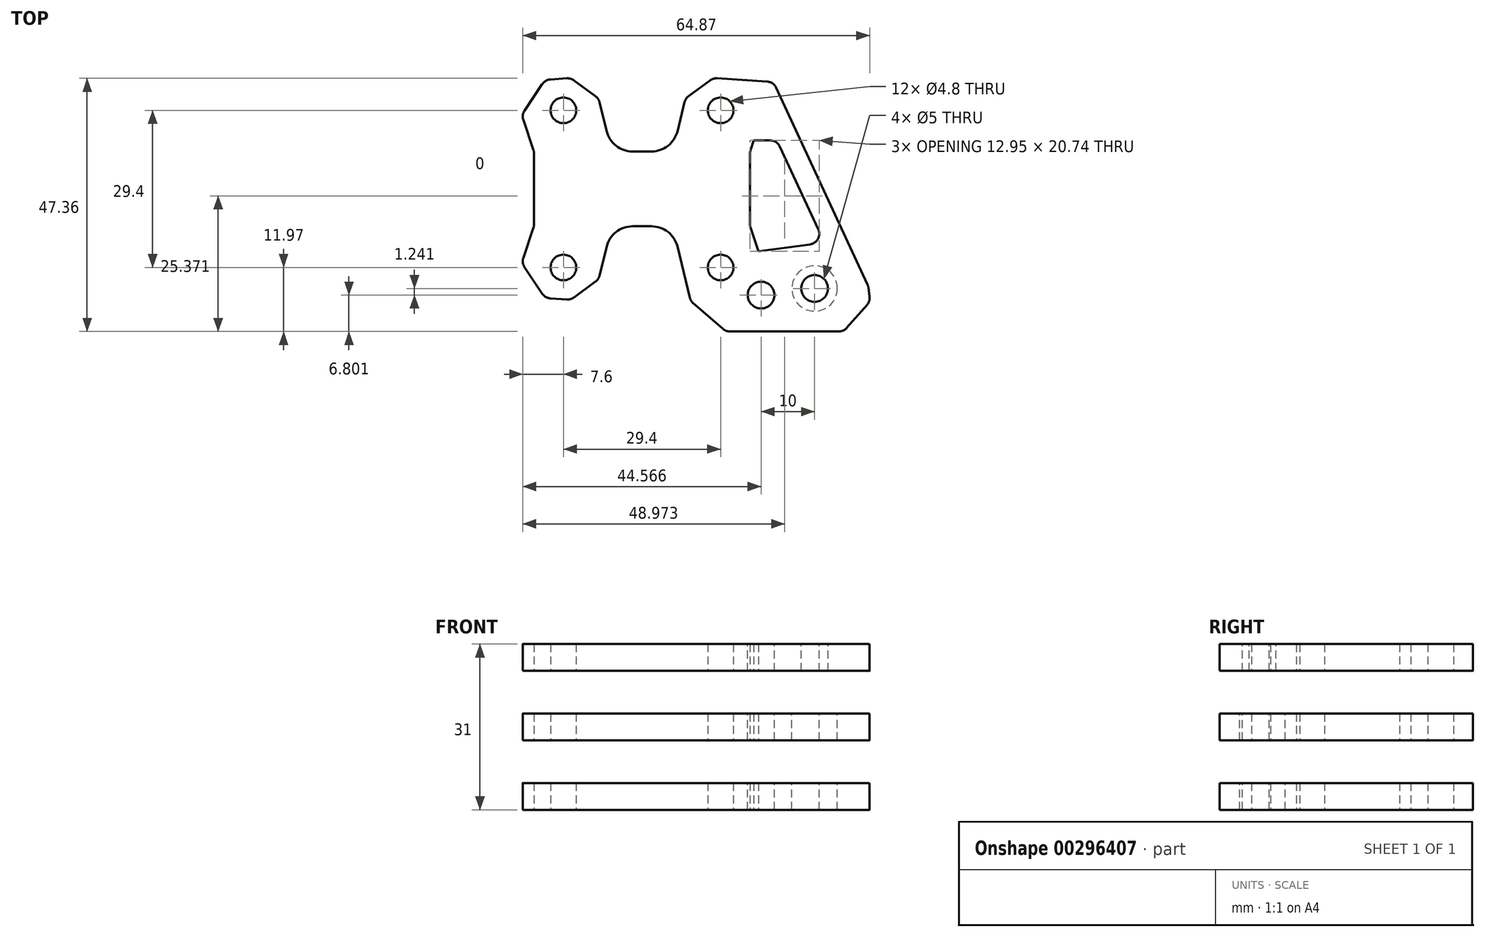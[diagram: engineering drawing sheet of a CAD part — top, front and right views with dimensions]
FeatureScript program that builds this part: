
annotation { "Feature Type Name" : "Feature", "Feature Type Description" : "" }
export const myFeature = defineFeature(function(context is Context, id is Id, definition is map)
    precondition{}
    {
        {
            var Q0;
            Q0=qCreatedBy(makeId("Top.planeOp"),FACE);
            var sketch = newSketch(context, id + "F0", { "sketchPlane" : qUnion([Q0])});
            skLineSegment(sketch, "E0.bottom", {"start": v(14.7, -14.7) * mm, "end": v(-14.7, -14.7) * mm, "construction": true});
            skLineSegment(sketch, "E0.top", {"start": v(14.7, 14.7) * mm, "end": v(-14.7, 14.7) * mm, "construction": true});
            skLineSegment(sketch, "E0.left", {"start": v(14.7, -14.7) * mm, "end": v(14.7, 14.7) * mm, "construction": true});
            skLineSegment(sketch, "E0.right", {"start": v(-14.7, -14.7) * mm, "end": v(-14.7, 14.7) * mm, "construction": true});
            skPoint(sketch, "E0.middle", {"position": v(0, 0) * mm});
            skLineSegment(sketch, "E1", {"start": v(-14.7, 5) * mm, "end": v(14.7, 5) * mm, "construction": true});
            skLineSegment(sketch, "E2.MirrorCS", {"start": v(-14.7, -5) * mm, "end": v(14.7, -5) * mm, "construction": true});
            skCircle(sketch, "E3", {"center": v(14.7, 14.7) * mm, "radius": 2.5 * mm, "construction": true});
            skCircle(sketch, "E4", {"center": v(14.7, 14.7) * mm, "radius": 9.7 * mm, "construction": true});
            skCircle(sketch, "E5.MirrorC", {"center": v(14.7, -14.7) * mm, "radius": 2.5 * mm, "construction": true});
            skCircle(sketch, "E6.MirrorC", {"center": v(14.7, -14.7) * mm, "radius": 9.7 * mm, "construction": true});
            skCircle(sketch, "E7.MirrorC", {"center": v(-14.7, 14.7) * mm, "radius": 9.7 * mm, "construction": true});
            skCircle(sketch, "E8.MirrorC", {"center": v(-14.7, 14.7) * mm, "radius": 2.5 * mm, "construction": true});
            skCircle(sketch, "E9.MirrorC", {"center": v(-14.7, -14.7) * mm, "radius": 9.7 * mm, "construction": true});
            skCircle(sketch, "E10.MirrorC", {"center": v(-14.7, -14.7) * mm, "radius": 2.5 * mm, "construction": true});
            skLineSegment(sketch, "E11", {"start": v(0, 7) * mm, "end": v(5.7, 7) * mm});
            skLineSegment(sketch, "E12", {"start": v(5.7, 7) * mm, "end": v(9.11, 21) * mm});
            skLineSegment(sketch, "E13", {"start": v(9.11, 21) * mm, "end": v(24.6, 20) * mm});
            skLineSegment(sketch, "E14", {"start": v(24.6, 20) * mm, "end": v(20.2, 7) * mm});
            skLineSegment(sketch, "E15", {"start": v(20.2, 7) * mm, "end": v(20.2, 0) * mm});
            skLineSegment(sketch, "E16", {"start": v(20.2, 0) * mm, "end": v(0, 0) * mm});
            skLineSegment(sketch, "E17", {"start": v(0, 7) * mm, "end": v(0, 0) * mm});
            skCircle(sketch, "E18", {"center": v(14.7, 14.7) * mm, "radius": 2.4 * mm});
            skSolve(sketch);
        }
        {
            var Q0;
            Q0=makeQuery(id+"F0.imprint","IMPRINT",FACE,{"disambiguationData":[TD([[makeQuery(id+"F0.imprint","IMPRINT",EDGE,{"derivedFrom":sQuery(id+"F0.wireOp",EDGE,"E11")}),-1.0]])]});
            extrude(context, id + "F1", {"entities" : qUnion([Q0]), "depth" : 5 * mm, "offsetDistance" : 25 * mm});
        }
        {
            var Q0;
            Q0=makeQuery(id+"F1.opExtrude","SWEPT_BODY",BODY,{"disambiguationData":[OSD([sQuery(id+"F0.wireOp",EDGE,"E11"),sQuery(id+"F0.wireOp",EDGE,"E12"),sQuery(id+"F0.wireOp",EDGE,"E13"),sQuery(id+"F0.wireOp",EDGE,"E14"),sQuery(id+"F0.wireOp",EDGE,"E15"),sQuery(id+"F0.wireOp",EDGE,"E16"),sQuery(id+"F0.wireOp",EDGE,"E17"),sQuery(id+"F0.wireOp",EDGE,"E18")])]});
            var Q1;
            Q1=makeQuery(id+"F1.opExtrude","SWEPT_FACE",FACE,{"disambiguationData":[OSD([sQuery(id+"F0.wireOp",EDGE,"E16")])]});
            mirror(context, id + "F2", {"operationType" : NewBodyOperationType.ADD, "entities" : qUnion([Q0]), "mirrorPlane" : qUnion([Q1])});
        }
        {
            var Q0;
            Q0=makeQuery(id+"F1.opExtrude","SWEPT_BODY",BODY,{"disambiguationData":[OSD([sQuery(id+"F0.wireOp",EDGE,"E11"),sQuery(id+"F0.wireOp",EDGE,"E12"),sQuery(id+"F0.wireOp",EDGE,"E13"),sQuery(id+"F0.wireOp",EDGE,"E14"),sQuery(id+"F0.wireOp",EDGE,"E15"),sQuery(id+"F0.wireOp",EDGE,"E16"),sQuery(id+"F0.wireOp",EDGE,"E17"),sQuery(id+"F0.wireOp",EDGE,"E18")])]});
            var Q1;
            {var subQ0=makeQuery(id+"F1.opExtrude","SWEPT_FACE",FACE,{"disambiguationData":[OSD([sQuery(id+"F0.wireOp",EDGE,"E17")])]});Q1=makeQuery(id+"F2.boolean.opBoolean","MERGE",FACE,{"derivedFrom":[subQ0,makeQuery(id+"F2.opPattern","COPY",FACE,{"derivedFrom":subQ0,"instanceName":"1"})]});}
            mirror(context, id + "F3", {"operationType" : NewBodyOperationType.ADD, "entities" : qUnion([Q0]), "mirrorPlane" : qUnion([Q1])});
        }
        {
            var Q0;
            Q0=qCreatedBy(makeId("Top.planeOp"),FACE);
            var sketch = newSketch(context, id + "F4", { "sketchPlane" : qUnion([Q0])});
            skLineSegment(sketch, "E19", {"start": v(0, 0) * mm, "end": v(45.1, -26.03) * mm, "construction": true});
            skPoint(sketch, "E20", {"position": v(32.27, -18.63) * mm});
            skCircle(sketch, "E21", {"center": v(32.27, -18.63) * mm, "radius": 5 * mm, "construction": true});
            skCircle(sketch, "E22", {"center": v(14.7, -14.7) * mm, "radius": 12 * mm, "construction": true});
            skLineSegment(sketch, "E23", {"start": v(24.6, 20) * mm, "end": v(42.3, -18.19) * mm});
            skLineSegment(sketch, "E24", {"start": v(42.3, -18.19) * mm, "end": v(43.42, -26.67) * mm});
            skLineSegment(sketch, "E25", {"start": v(43.42, -26.67) * mm, "end": v(15.65, -26.67) * mm});
            skLineSegment(sketch, "E26", {"start": v(15.65, -26.67) * mm, "end": v(9.11, -21) * mm});
            skLineSegment(sketch, "E27", {"start": v(25.26, 9.07) * mm, "end": v(34.1, -10.02) * mm});
            skLineSegment(sketch, "E28", {"start": v(34.1, -10.02) * mm, "end": v(21.78, -11.67) * mm});
            skLineSegment(sketch, "E29", {"start": v(25.26, 9.07) * mm, "end": v(20.9, 9.07) * mm});
            skLineSegment(sketch, "E30", {"start": v(24.6, 20) * mm, "end": v(20.9, 9.07) * mm});
            skLineSegment(sketch, "E31", {"start": v(9.11, -21) * mm, "end": v(20.23, -18.7) * mm});
            skLineSegment(sketch, "E32", {"start": v(20.23, -18.7) * mm, "end": v(21.78, -11.67) * mm});
            skSolve(sketch);
        }
        {
            var Q0;
            Q0=makeQuery(id+"F4.imprint","IMPRINT",FACE,{"disambiguationData":[TD([[makeQuery(id+"F4.imprint","IMPRINT",EDGE,{"derivedFrom":sQuery(id+"F4.wireOp",EDGE,"E23")}),-1.0]])]});
            var Q1;
            {var subQ0=makeQuery(id+"F1.opExtrude","CAP_FACE",FACE,{"disambiguationData":[OSD([sQuery(id+"F0.wireOp",EDGE,"E11"),sQuery(id+"F0.wireOp",EDGE,"E12"),sQuery(id+"F0.wireOp",EDGE,"E13"),sQuery(id+"F0.wireOp",EDGE,"E14"),sQuery(id+"F0.wireOp",EDGE,"E15"),sQuery(id+"F0.wireOp",EDGE,"E16"),sQuery(id+"F0.wireOp",EDGE,"E17"),sQuery(id+"F0.wireOp",EDGE,"E18")])],"isStart":false});var subQ1=makeQuery(id+"F2.boolean.opBoolean","MERGE",FACE,{"derivedFrom":[subQ0,makeQuery(id+"F2.opPattern","COPY",FACE,{"derivedFrom":subQ0,"instanceName":"1"})]});Q1=makeQuery(id+"F3.boolean.opBoolean","MERGE",FACE,{"derivedFrom":[subQ1,makeQuery(id+"F3.opPattern","COPY",FACE,{"derivedFrom":subQ1,"instanceName":"1"})]});}
            extrude(context, id + "F5", {"entities" : qUnion([Q0]), "operationType" : NewBodyOperationType.ADD, "endBound" : BoundingType.UP_TO_SURFACE, "depth" : 25 * mm, "endBoundEntityFace" : qUnion([Q1]), "offsetDistance" : 25 * mm});
        }
        {
            var Q0;
            Q0=makeQuery(id+"F3.opPattern","COPY",EDGE,{"derivedFrom":makeQuery(id+"F1.opExtrude","SWEPT_EDGE",EDGE,{"disambiguationData":[OSD([sQuery(id+"F0.wireOp",EDGE,"E13"),sQuery(id+"F0.wireOp",EDGE,"E14")])]}),"instanceName":"1"});
            var Q1;
            Q1=makeQuery(id+"F3.opPattern","COPY",EDGE,{"derivedFrom":makeQuery(id+"F2.opPattern","COPY",EDGE,{"derivedFrom":makeQuery(id+"F1.opExtrude","SWEPT_EDGE",EDGE,{"disambiguationData":[OSD([sQuery(id+"F0.wireOp",EDGE,"E13"),sQuery(id+"F0.wireOp",EDGE,"E14")])]}),"instanceName":"1"}),"instanceName":"1"});
            var Q2;
            Q2=makeQuery(id+"F3.opPattern","COPY",EDGE,{"derivedFrom":makeQuery(id+"F2.opPattern","COPY",EDGE,{"derivedFrom":makeQuery(id+"F1.opExtrude","SWEPT_EDGE",EDGE,{"disambiguationData":[OSD([sQuery(id+"F0.wireOp",EDGE,"E12"),sQuery(id+"F0.wireOp",EDGE,"E13")])]}),"instanceName":"1"}),"instanceName":"1"});
            var Q3;
            Q3=makeQuery(id+"F3.opPattern","COPY",EDGE,{"derivedFrom":makeQuery(id+"F1.opExtrude","SWEPT_EDGE",EDGE,{"disambiguationData":[OSD([sQuery(id+"F0.wireOp",EDGE,"E12"),sQuery(id+"F0.wireOp",EDGE,"E13")])]}),"instanceName":"1"});
            var Q4;
            Q4=makeQuery(id+"F1.opExtrude","SWEPT_EDGE",EDGE,{"disambiguationData":[OSD([sQuery(id+"F0.wireOp",EDGE,"E12"),sQuery(id+"F0.wireOp",EDGE,"E13")])]});
            var Q5;
            Q5=makeQuery(id+"F5.opExtrude","SWEPT_EDGE",EDGE,{"disambiguationData":[OSD([sQuery(id+"F4.wireOp",EDGE,"E24"),sQuery(id+"F4.wireOp",EDGE,"E25")])]});
            chamfer(context, id + "F6", {"entities" : qUnion([Q0, Q1, Q2, Q3, Q4, Q5]), "width" : 5 * mm, "tangentPropagation" : true});
        }
        {
            var Q0;
            Q0=makeQuery(id+"F3.opPattern","COPY",EDGE,{"derivedFrom":makeQuery(id+"F1.opExtrude","SWEPT_EDGE",EDGE,{"disambiguationData":[OSD([sQuery(id+"F0.wireOp",EDGE,"E11"),sQuery(id+"F0.wireOp",EDGE,"E12")])]}),"instanceName":"1"});
            var Q1;
            Q1=makeQuery(id+"F1.opExtrude","SWEPT_EDGE",EDGE,{"disambiguationData":[OSD([sQuery(id+"F0.wireOp",EDGE,"E11"),sQuery(id+"F0.wireOp",EDGE,"E12")])]});
            var Q2;
            Q2=makeQuery(id+"F2.opPattern","COPY",EDGE,{"derivedFrom":makeQuery(id+"F1.opExtrude","SWEPT_EDGE",EDGE,{"disambiguationData":[OSD([sQuery(id+"F0.wireOp",EDGE,"E11"),sQuery(id+"F0.wireOp",EDGE,"E12")])]}),"instanceName":"1"});
            var Q3;
            Q3=makeQuery(id+"F3.opPattern","COPY",EDGE,{"derivedFrom":makeQuery(id+"F2.opPattern","COPY",EDGE,{"derivedFrom":makeQuery(id+"F1.opExtrude","SWEPT_EDGE",EDGE,{"disambiguationData":[OSD([sQuery(id+"F0.wireOp",EDGE,"E11"),sQuery(id+"F0.wireOp",EDGE,"E12")])]}),"instanceName":"1"}),"instanceName":"1"});
            fillet(context, id + "F7", {"entities" : qUnion([Q0, Q1, Q2, Q3]), "radius" : 5 * mm, "tangentPropagation" : true, "allowEdgeOverflow" : false});
        }
        {
            var Q0;
            {var subQ0=sQuery(id+"F0.wireOp",EDGE,"E14");Q0=makeQuery(id+"F6.opChamfer","BLEND_EDGE",EDGE,{"blendedFrom":[makeQuery(id+"F3.opPattern","COPY",EDGE,{"derivedFrom":makeQuery(id+"F1.opExtrude","SWEPT_EDGE",EDGE,{"disambiguationData":[OSD([sQuery(id+"F0.wireOp",EDGE,"E13"),subQ0])]}),"instanceName":"1"}),makeQuery(id+"F3.opPattern","COPY",FACE,{"derivedFrom":makeQuery(id+"F1.opExtrude","SWEPT_FACE",FACE,{"disambiguationData":[OSD([subQ0])]}),"instanceName":"1"})],"blendedInto":[makeQuery(id+"F3.opPattern","COPY",FACE,{"derivedFrom":makeQuery(id+"F1.opExtrude","SWEPT_FACE",FACE,{"disambiguationData":[OSD([subQ0])]}),"instanceName":"1"})]});}
            var Q1;
            Q1=makeQuery(id+"F3.opPattern","COPY",EDGE,{"derivedFrom":makeQuery(id+"F1.opExtrude","SWEPT_EDGE",EDGE,{"disambiguationData":[OSD([sQuery(id+"F0.wireOp",EDGE,"E14"),sQuery(id+"F0.wireOp",EDGE,"E15")])]}),"instanceName":"1"});
            var Q2;
            Q2=makeQuery(id+"F3.opPattern","COPY",EDGE,{"derivedFrom":makeQuery(id+"F2.opPattern","COPY",EDGE,{"derivedFrom":makeQuery(id+"F1.opExtrude","SWEPT_EDGE",EDGE,{"disambiguationData":[OSD([sQuery(id+"F0.wireOp",EDGE,"E14"),sQuery(id+"F0.wireOp",EDGE,"E15")])]}),"instanceName":"1"}),"instanceName":"1"});
            var Q3;
            {var subQ0=sQuery(id+"F0.wireOp",EDGE,"E14");Q3=makeQuery(id+"F6.opChamfer","BLEND_EDGE",EDGE,{"blendedFrom":[makeQuery(id+"F3.opPattern","COPY",EDGE,{"derivedFrom":makeQuery(id+"F2.opPattern","COPY",EDGE,{"derivedFrom":makeQuery(id+"F1.opExtrude","SWEPT_EDGE",EDGE,{"disambiguationData":[OSD([sQuery(id+"F0.wireOp",EDGE,"E13"),subQ0])]}),"instanceName":"1"}),"instanceName":"1"}),makeQuery(id+"F3.opPattern","COPY",FACE,{"derivedFrom":makeQuery(id+"F2.opPattern","COPY",FACE,{"derivedFrom":makeQuery(id+"F1.opExtrude","SWEPT_FACE",FACE,{"disambiguationData":[OSD([subQ0])]}),"instanceName":"1"}),"instanceName":"1"})],"blendedInto":[makeQuery(id+"F3.opPattern","COPY",FACE,{"derivedFrom":makeQuery(id+"F2.opPattern","COPY",FACE,{"derivedFrom":makeQuery(id+"F1.opExtrude","SWEPT_FACE",FACE,{"disambiguationData":[OSD([subQ0])]}),"instanceName":"1"}),"instanceName":"1"})]});}
            var Q4;
            {var subQ0=sQuery(id+"F0.wireOp",EDGE,"E13");Q4=makeQuery(id+"F6.opChamfer","BLEND_EDGE",EDGE,{"blendedFrom":[makeQuery(id+"F3.opPattern","COPY",EDGE,{"derivedFrom":makeQuery(id+"F2.opPattern","COPY",EDGE,{"derivedFrom":makeQuery(id+"F1.opExtrude","SWEPT_EDGE",EDGE,{"disambiguationData":[OSD([subQ0,sQuery(id+"F0.wireOp",EDGE,"E14")])]}),"instanceName":"1"}),"instanceName":"1"}),makeQuery(id+"F3.opPattern","COPY",FACE,{"derivedFrom":makeQuery(id+"F2.opPattern","COPY",FACE,{"derivedFrom":makeQuery(id+"F1.opExtrude","SWEPT_FACE",FACE,{"disambiguationData":[OSD([subQ0])]}),"instanceName":"1"}),"instanceName":"1"})],"blendedInto":[makeQuery(id+"F3.opPattern","COPY",FACE,{"derivedFrom":makeQuery(id+"F2.opPattern","COPY",FACE,{"derivedFrom":makeQuery(id+"F1.opExtrude","SWEPT_FACE",FACE,{"disambiguationData":[OSD([subQ0])]}),"instanceName":"1"}),"instanceName":"1"})]});}
            var Q5;
            {var subQ0=sQuery(id+"F0.wireOp",EDGE,"E13");Q5=makeQuery(id+"F6.opChamfer","BLEND_EDGE",EDGE,{"blendedFrom":[makeQuery(id+"F3.opPattern","COPY",EDGE,{"derivedFrom":makeQuery(id+"F2.opPattern","COPY",EDGE,{"derivedFrom":makeQuery(id+"F1.opExtrude","SWEPT_EDGE",EDGE,{"disambiguationData":[OSD([sQuery(id+"F0.wireOp",EDGE,"E12"),subQ0])]}),"instanceName":"1"}),"instanceName":"1"}),makeQuery(id+"F3.opPattern","COPY",FACE,{"derivedFrom":makeQuery(id+"F2.opPattern","COPY",FACE,{"derivedFrom":makeQuery(id+"F1.opExtrude","SWEPT_FACE",FACE,{"disambiguationData":[OSD([subQ0])]}),"instanceName":"1"}),"instanceName":"1"})],"blendedInto":[makeQuery(id+"F3.opPattern","COPY",FACE,{"derivedFrom":makeQuery(id+"F2.opPattern","COPY",FACE,{"derivedFrom":makeQuery(id+"F1.opExtrude","SWEPT_FACE",FACE,{"disambiguationData":[OSD([subQ0])]}),"instanceName":"1"}),"instanceName":"1"})]});}
            var Q6;
            {var subQ0=sQuery(id+"F0.wireOp",EDGE,"E12");Q6=makeQuery(id+"F6.opChamfer","BLEND_EDGE",EDGE,{"blendedFrom":[makeQuery(id+"F3.opPattern","COPY",EDGE,{"derivedFrom":makeQuery(id+"F2.opPattern","COPY",EDGE,{"derivedFrom":makeQuery(id+"F1.opExtrude","SWEPT_EDGE",EDGE,{"disambiguationData":[OSD([subQ0,sQuery(id+"F0.wireOp",EDGE,"E13")])]}),"instanceName":"1"}),"instanceName":"1"}),makeQuery(id+"F3.opPattern","COPY",FACE,{"derivedFrom":makeQuery(id+"F2.opPattern","COPY",FACE,{"derivedFrom":makeQuery(id+"F1.opExtrude","SWEPT_FACE",FACE,{"disambiguationData":[OSD([subQ0])]}),"instanceName":"1"}),"instanceName":"1"})],"blendedInto":[makeQuery(id+"F3.opPattern","COPY",FACE,{"derivedFrom":makeQuery(id+"F2.opPattern","COPY",FACE,{"derivedFrom":makeQuery(id+"F1.opExtrude","SWEPT_FACE",FACE,{"disambiguationData":[OSD([subQ0])]}),"instanceName":"1"}),"instanceName":"1"})]});}
            var Q7;
            Q7=makeQuery(id+"F5.boolean.opBoolean","MERGE",EDGE,{"derivedFrom":[makeQuery(id+"F2.opPattern","COPY",EDGE,{"derivedFrom":makeQuery(id+"F1.opExtrude","SWEPT_EDGE",EDGE,{"disambiguationData":[OSD([sQuery(id+"F0.wireOp",EDGE,"E12"),sQuery(id+"F0.wireOp",EDGE,"E13")])]}),"instanceName":"1"}),makeQuery(id+"F5.opExtrude","SWEPT_EDGE",EDGE,{"disambiguationData":[OSD([sQuery(id+"F4.wireOp",EDGE,"E26"),sQuery(id+"F4.wireOp",EDGE,"E31")])]})]});
            var Q8;
            Q8=makeQuery(id+"F5.opExtrude","SWEPT_EDGE",EDGE,{"disambiguationData":[OSD([sQuery(id+"F4.wireOp",EDGE,"E25"),sQuery(id+"F4.wireOp",EDGE,"E26")])]});
            var Q9;
            {var subQ0=sQuery(id+"F4.wireOp",EDGE,"E25");Q9=makeQuery(id+"F6.opChamfer","BLEND_EDGE",EDGE,{"blendedFrom":[makeQuery(id+"F5.opExtrude","SWEPT_EDGE",EDGE,{"disambiguationData":[OSD([sQuery(id+"F4.wireOp",EDGE,"E24"),subQ0])]}),makeQuery(id+"F5.opExtrude","SWEPT_FACE",FACE,{"disambiguationData":[OSD([subQ0])]})],"blendedInto":[makeQuery(id+"F5.opExtrude","SWEPT_FACE",FACE,{"disambiguationData":[OSD([subQ0])]})]});}
            var Q10;
            {var subQ0=sQuery(id+"F4.wireOp",EDGE,"E24");Q10=makeQuery(id+"F6.opChamfer","BLEND_EDGE",EDGE,{"blendedFrom":[makeQuery(id+"F5.opExtrude","SWEPT_EDGE",EDGE,{"disambiguationData":[OSD([subQ0,sQuery(id+"F4.wireOp",EDGE,"E25")])]}),makeQuery(id+"F5.opExtrude","SWEPT_FACE",FACE,{"disambiguationData":[OSD([subQ0])]})],"blendedInto":[makeQuery(id+"F5.opExtrude","SWEPT_FACE",FACE,{"disambiguationData":[OSD([subQ0])]})]});}
            var Q11;
            Q11=makeQuery(id+"F5.opExtrude","SWEPT_EDGE",EDGE,{"disambiguationData":[OSD([sQuery(id+"F4.wireOp",EDGE,"E23"),sQuery(id+"F4.wireOp",EDGE,"E24")])]});
            var Q12;
            Q12=makeQuery(id+"F5.boolean.opBoolean","MERGE",EDGE,{"derivedFrom":[makeQuery(id+"F1.opExtrude","SWEPT_EDGE",EDGE,{"disambiguationData":[OSD([sQuery(id+"F0.wireOp",EDGE,"E13"),sQuery(id+"F0.wireOp",EDGE,"E14")])]}),makeQuery(id+"F5.opExtrude","SWEPT_EDGE",EDGE,{"disambiguationData":[OSD([sQuery(id+"F4.wireOp",EDGE,"E23"),sQuery(id+"F4.wireOp",EDGE,"E30")])]})]});
            var Q13;
            {var subQ0=sQuery(id+"F0.wireOp",EDGE,"E13");Q13=makeQuery(id+"F6.opChamfer","BLEND_EDGE",EDGE,{"blendedFrom":[makeQuery(id+"F1.opExtrude","SWEPT_EDGE",EDGE,{"disambiguationData":[OSD([sQuery(id+"F0.wireOp",EDGE,"E12"),subQ0])]}),makeQuery(id+"F1.opExtrude","SWEPT_FACE",FACE,{"disambiguationData":[OSD([subQ0])]})],"blendedInto":[makeQuery(id+"F1.opExtrude","SWEPT_FACE",FACE,{"disambiguationData":[OSD([subQ0])]})]});}
            var Q14;
            {var subQ0=sQuery(id+"F0.wireOp",EDGE,"E12");Q14=makeQuery(id+"F6.opChamfer","BLEND_EDGE",EDGE,{"blendedFrom":[makeQuery(id+"F1.opExtrude","SWEPT_EDGE",EDGE,{"disambiguationData":[OSD([subQ0,sQuery(id+"F0.wireOp",EDGE,"E13")])]}),makeQuery(id+"F1.opExtrude","SWEPT_FACE",FACE,{"disambiguationData":[OSD([subQ0])]})],"blendedInto":[makeQuery(id+"F1.opExtrude","SWEPT_FACE",FACE,{"disambiguationData":[OSD([subQ0])]})]});}
            var Q15;
            {var subQ0=sQuery(id+"F0.wireOp",EDGE,"E12");Q15=makeQuery(id+"F6.opChamfer","BLEND_EDGE",EDGE,{"blendedFrom":[makeQuery(id+"F3.opPattern","COPY",EDGE,{"derivedFrom":makeQuery(id+"F1.opExtrude","SWEPT_EDGE",EDGE,{"disambiguationData":[OSD([subQ0,sQuery(id+"F0.wireOp",EDGE,"E13")])]}),"instanceName":"1"}),makeQuery(id+"F3.opPattern","COPY",FACE,{"derivedFrom":makeQuery(id+"F1.opExtrude","SWEPT_FACE",FACE,{"disambiguationData":[OSD([subQ0])]}),"instanceName":"1"})],"blendedInto":[makeQuery(id+"F3.opPattern","COPY",FACE,{"derivedFrom":makeQuery(id+"F1.opExtrude","SWEPT_FACE",FACE,{"disambiguationData":[OSD([subQ0])]}),"instanceName":"1"})]});}
            var Q16;
            {var subQ0=sQuery(id+"F0.wireOp",EDGE,"E13");Q16=makeQuery(id+"F6.opChamfer","BLEND_EDGE",EDGE,{"blendedFrom":[makeQuery(id+"F3.opPattern","COPY",EDGE,{"derivedFrom":makeQuery(id+"F1.opExtrude","SWEPT_EDGE",EDGE,{"disambiguationData":[OSD([sQuery(id+"F0.wireOp",EDGE,"E12"),subQ0])]}),"instanceName":"1"}),makeQuery(id+"F3.opPattern","COPY",FACE,{"derivedFrom":makeQuery(id+"F1.opExtrude","SWEPT_FACE",FACE,{"disambiguationData":[OSD([subQ0])]}),"instanceName":"1"})],"blendedInto":[makeQuery(id+"F3.opPattern","COPY",FACE,{"derivedFrom":makeQuery(id+"F1.opExtrude","SWEPT_FACE",FACE,{"disambiguationData":[OSD([subQ0])]}),"instanceName":"1"})]});}
            var Q17;
            {var subQ0=sQuery(id+"F0.wireOp",EDGE,"E13");Q17=makeQuery(id+"F6.opChamfer","BLEND_EDGE",EDGE,{"blendedFrom":[makeQuery(id+"F3.opPattern","COPY",EDGE,{"derivedFrom":makeQuery(id+"F1.opExtrude","SWEPT_EDGE",EDGE,{"disambiguationData":[OSD([subQ0,sQuery(id+"F0.wireOp",EDGE,"E14")])]}),"instanceName":"1"}),makeQuery(id+"F3.opPattern","COPY",FACE,{"derivedFrom":makeQuery(id+"F1.opExtrude","SWEPT_FACE",FACE,{"disambiguationData":[OSD([subQ0])]}),"instanceName":"1"})],"blendedInto":[makeQuery(id+"F3.opPattern","COPY",FACE,{"derivedFrom":makeQuery(id+"F1.opExtrude","SWEPT_FACE",FACE,{"disambiguationData":[OSD([subQ0])]}),"instanceName":"1"})]});}
            fillet(context, id + "F8", {"entities" : qUnion([Q0, Q1, Q2, Q3, Q4, Q5, Q6, Q7, Q8, Q9, Q10, Q11, Q12, Q13, Q14, Q15, Q16, Q17]), "radius" : 2 * mm, "tangentPropagation" : true, "allowEdgeOverflow" : false});
        }
        {
            var Q0;
            Q0=makeQuery(id+"F5.opExtrude","SWEPT_EDGE",EDGE,{"disambiguationData":[OSD([sQuery(id+"F4.wireOp",EDGE,"E29"),sQuery(id+"F4.wireOp",EDGE,"E30")])]});
            var Q1;
            Q1=makeQuery(id+"F2.opPattern","COPY",EDGE,{"derivedFrom":makeQuery(id+"F1.opExtrude","SWEPT_EDGE",EDGE,{"disambiguationData":[OSD([sQuery(id+"F0.wireOp",EDGE,"E14"),sQuery(id+"F0.wireOp",EDGE,"E15")])]}),"instanceName":"1"});
            var Q2;
            Q2=makeQuery(id+"F5.opExtrude","SWEPT_EDGE",EDGE,{"disambiguationData":[OSD([sQuery(id+"F4.wireOp",EDGE,"E28"),sQuery(id+"F4.wireOp",EDGE,"E32")])]});
            var Q3;
            Q3=makeQuery(id+"F5.opExtrude","SWEPT_EDGE",EDGE,{"disambiguationData":[OSD([sQuery(id+"F4.wireOp",EDGE,"E27"),sQuery(id+"F4.wireOp",EDGE,"E28")])]});
            var Q4;
            Q4=makeQuery(id+"F5.opExtrude","SWEPT_EDGE",EDGE,{"disambiguationData":[OSD([sQuery(id+"F4.wireOp",EDGE,"E27"),sQuery(id+"F4.wireOp",EDGE,"E29")])]});
            var Q5;
            Q5=makeQuery(id+"F1.opExtrude","SWEPT_EDGE",EDGE,{"disambiguationData":[OSD([sQuery(id+"F0.wireOp",EDGE,"E14"),sQuery(id+"F0.wireOp",EDGE,"E15")])]});
            fillet(context, id + "F9", {"entities" : qUnion([Q0, Q1, Q2, Q3, Q4, Q5]), "radius" : 2 * mm, "tangentPropagation" : true, "allowEdgeOverflow" : false});
        }
        {
            var Q0;
            {var subQ0=makeQuery(id+"F1.opExtrude","CAP_FACE",FACE,{"disambiguationData":[OSD([sQuery(id+"F0.wireOp",EDGE,"E11"),sQuery(id+"F0.wireOp",EDGE,"E12"),sQuery(id+"F0.wireOp",EDGE,"E13"),sQuery(id+"F0.wireOp",EDGE,"E14"),sQuery(id+"F0.wireOp",EDGE,"E15"),sQuery(id+"F0.wireOp",EDGE,"E16"),sQuery(id+"F0.wireOp",EDGE,"E17"),sQuery(id+"F0.wireOp",EDGE,"E18")])],"isStart":false});var subQ1=makeQuery(id+"F2.boolean.opBoolean","MERGE",FACE,{"derivedFrom":[subQ0,makeQuery(id+"F2.opPattern","COPY",FACE,{"derivedFrom":subQ0,"instanceName":"1"})]});Q0=makeQuery(id+"F5.boolean.opBoolean","MERGE",FACE,{"derivedFrom":[makeQuery(id+"F3.boolean.opBoolean","MERGE",FACE,{"derivedFrom":[subQ1,makeQuery(id+"F3.opPattern","COPY",FACE,{"derivedFrom":subQ1,"instanceName":"1"})]}),makeQuery(id+"F5.opExtrude","CAP_FACE",FACE,{"disambiguationData":[OSD([sQuery(id+"F4.wireOp",EDGE,"E23"),sQuery(id+"F4.wireOp",EDGE,"E24"),sQuery(id+"F4.wireOp",EDGE,"E25"),sQuery(id+"F4.wireOp",EDGE,"E26"),sQuery(id+"F4.wireOp",EDGE,"E27"),sQuery(id+"F4.wireOp",EDGE,"E28"),sQuery(id+"F4.wireOp",EDGE,"E29"),sQuery(id+"F4.wireOp",EDGE,"E30"),sQuery(id+"F4.wireOp",EDGE,"E31"),sQuery(id+"F4.wireOp",EDGE,"E32")])],"isStart":false})]});}
            var sketch = newSketch(context, id + "F10", { "sketchPlane" : qUnion([Q0])});
            skCircle(sketch, "E33", {"center": v(22.27, -19.87) * mm, "radius": 2.5 * mm});
            skSolve(sketch);
        }
        {
            var Q0;
            Q0=makeQuery(id+"F10.imprint","IMPRINT",FACE,{"disambiguationData":[TD([[makeQuery(id+"F10.imprint","IMPRINT",EDGE,{"derivedFrom":sQuery(id+"F10.wireOp",EDGE,"E33")}),1.0]])]});
            extrude(context, id + "F11", {"entities" : qUnion([Q0]), "operationType" : NewBodyOperationType.REMOVE, "endBound" : BoundingType.UP_TO_NEXT, "oppositeDirection" : true, "depth" : 25 * mm, "offsetDistance" : 25 * mm});
        }
        {
            var Q0;
            Q0=makeQuery(id+"F1.opExtrude","SWEPT_BODY",BODY,{"disambiguationData":[OSD([sQuery(id+"F0.wireOp",EDGE,"E11"),sQuery(id+"F0.wireOp",EDGE,"E12"),sQuery(id+"F0.wireOp",EDGE,"E13"),sQuery(id+"F0.wireOp",EDGE,"E14"),sQuery(id+"F0.wireOp",EDGE,"E15"),sQuery(id+"F0.wireOp",EDGE,"E16"),sQuery(id+"F0.wireOp",EDGE,"E17"),sQuery(id+"F0.wireOp",EDGE,"E18")])]});
            transform(context, id + "F12", {"entities" : qUnion([Q0]), "transformType" : TransformType.TRANSLATION_3D, "dx" : 0 * mm, "dy" : 0 * mm, "dz" : 26 * mm, "makeCopy" : true});
        }
        {
            var Q0;
            Q0=sQuery(id+"F4.wireOp",VERTEX,"E20");
            var Q1;
            Q1=makeQuery(id+"F1.opExtrude","SWEPT_BODY",BODY,{"disambiguationData":[OSD([sQuery(id+"F0.wireOp",EDGE,"E11"),sQuery(id+"F0.wireOp",EDGE,"E12"),sQuery(id+"F0.wireOp",EDGE,"E13"),sQuery(id+"F0.wireOp",EDGE,"E14"),sQuery(id+"F0.wireOp",EDGE,"E15"),sQuery(id+"F0.wireOp",EDGE,"E16"),sQuery(id+"F0.wireOp",EDGE,"E17"),sQuery(id+"F0.wireOp",EDGE,"E18")])]});
            hole(context, id + "F13", {"style" : HoleStyle.SIMPLE, "endStyle" : HoleEndStyle.THROUGH, "oppositeDirection" : true, "standardTappedOrClearance" : lookupTablePath({ "standard" : "ISO", "engagement" : "75%", "pitch" : "1.5 mm", "size" : "M10", "type" : "Tapped" }), "standardBlindInLast" : lookupTablePath({ "standard" : "ISO", "engagement" : "75%", "pitch" : "1.5 mm", "size" : "M10", "type" : "Tapped" }), "holeDiameter" : 8.5 * mm, "majorDiameter" : 10 * mm, "showTappedDepth" : true, "isTappedThrough" : true, "tappedDepth" : 12 * mm, "tapClearance" : 3, "locations" : qUnion([Q0]), "scope" : qUnion([Q1])});
        }
        {
            var Q0;
            Q0=makeQuery(id+"F1.opExtrude","SWEPT_BODY",BODY,{"disambiguationData":[OSD([sQuery(id+"F0.wireOp",EDGE,"E11"),sQuery(id+"F0.wireOp",EDGE,"E12"),sQuery(id+"F0.wireOp",EDGE,"E13"),sQuery(id+"F0.wireOp",EDGE,"E14"),sQuery(id+"F0.wireOp",EDGE,"E15"),sQuery(id+"F0.wireOp",EDGE,"E16"),sQuery(id+"F0.wireOp",EDGE,"E17"),sQuery(id+"F0.wireOp",EDGE,"E18")])]});
            transform(context, id + "F14", {"entities" : qUnion([Q0]), "transformType" : TransformType.TRANSLATION_3D, "dx" : 0 * mm, "dy" : 0 * mm, "dz" : 13 * mm, "makeCopy" : true});
        }
        {
            var Q0;
            Q0=sQuery(id+"F4.wireOp",VERTEX,"E20");
            var Q1;
            Q1=makeQuery(id+"F12.opPattern","COPY",BODY,{"derivedFrom":makeQuery(id+"F1.opExtrude","SWEPT_BODY",BODY,{"disambiguationData":[OSD([sQuery(id+"F0.wireOp",EDGE,"E11"),sQuery(id+"F0.wireOp",EDGE,"E12"),sQuery(id+"F0.wireOp",EDGE,"E13"),sQuery(id+"F0.wireOp",EDGE,"E14"),sQuery(id+"F0.wireOp",EDGE,"E15"),sQuery(id+"F0.wireOp",EDGE,"E16"),sQuery(id+"F0.wireOp",EDGE,"E17"),sQuery(id+"F0.wireOp",EDGE,"E18")])]}),"instanceName":"1"});
            hole(context, id + "F15", {"style" : HoleStyle.SIMPLE, "endStyle" : HoleEndStyle.THROUGH, "oppositeDirection" : true, "standardTappedOrClearance" : lookupTablePath({ "standard" : "ISO", "engagement" : "75%", "pitch" : "1 mm", "size" : "M6", "type" : "Tapped" }), "standardBlindInLast" : lookupTablePath({ "standard" : "ISO", "engagement" : "75%", "pitch" : "1 mm", "size" : "M6", "type" : "Tapped" }), "holeDiameter" : 5 * mm, "majorDiameter" : 6 * mm, "showTappedDepth" : true, "isTappedThrough" : true, "tappedDepth" : 12 * mm, "tapClearance" : 3, "locations" : qUnion([Q0]), "scope" : qUnion([Q1])});
        }
    });
